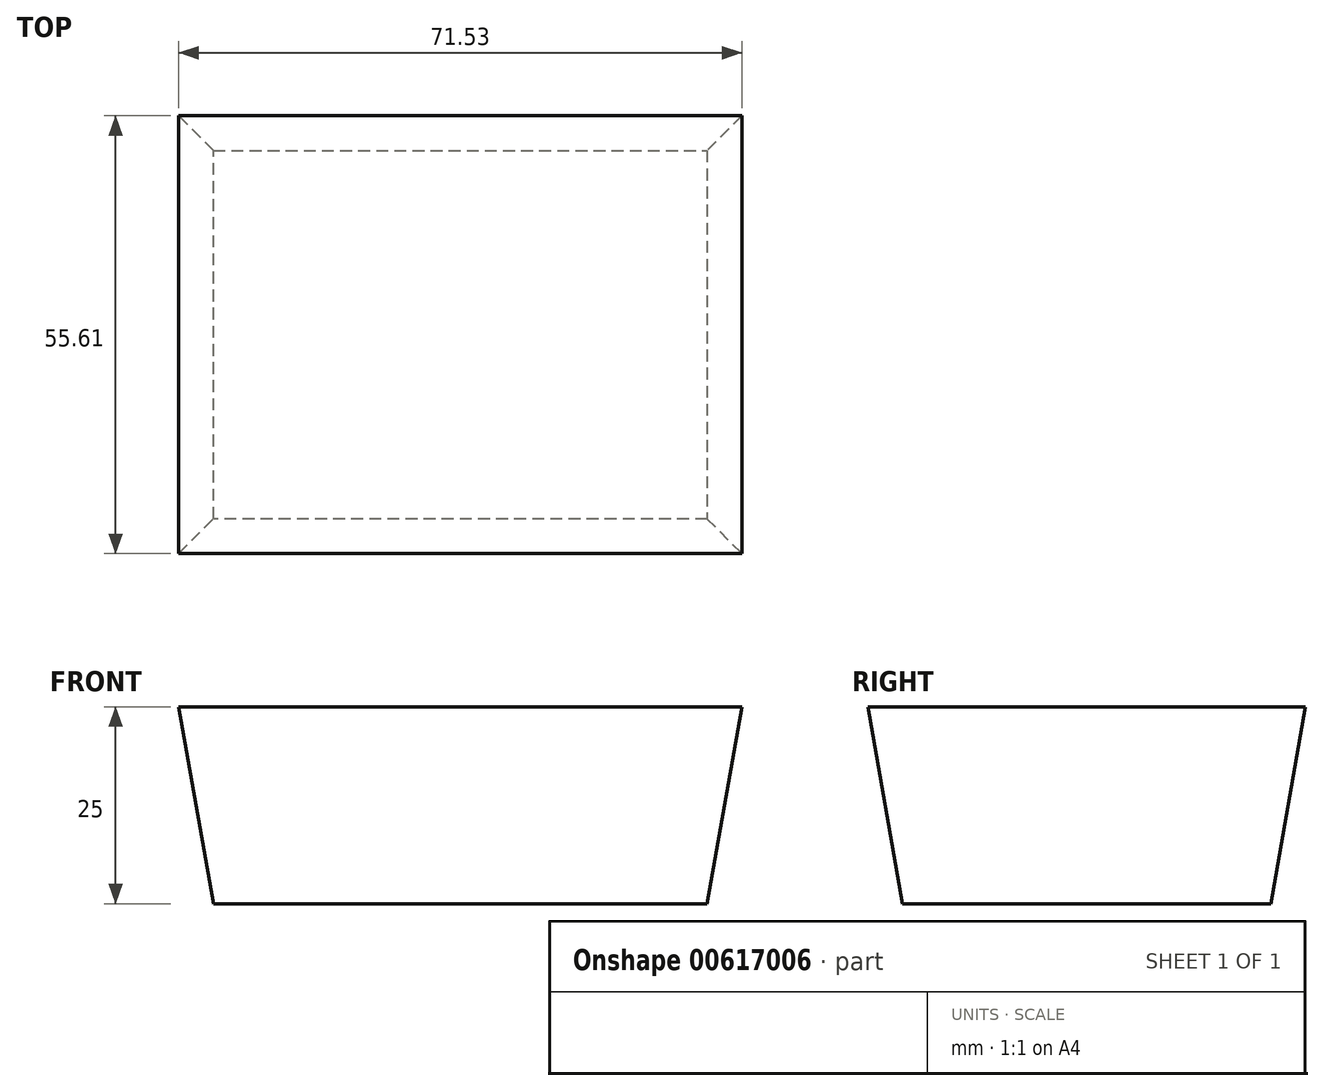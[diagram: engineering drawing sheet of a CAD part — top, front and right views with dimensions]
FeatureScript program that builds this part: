
annotation { "Feature Type Name" : "Feature", "Feature Type Description" : "" }
export const myFeature = defineFeature(function(context is Context, id is Id, definition is map)
    precondition{}
    {
        {
            var Q0;
            Q0=qCreatedBy(makeId("Top.planeOp"),FACE);
            var sketch = newSketch(context, id + "F0", { "sketchPlane" : qUnion([Q0])});
            skLineSegment(sketch, "E0.bottom", {"start": v(-32.52, 24.59) * mm, "end": v(30.2, 24.59) * mm});
            skLineSegment(sketch, "E0.top", {"start": v(-32.52, -22.2) * mm, "end": v(30.2, -22.2) * mm});
            skLineSegment(sketch, "E0.left", {"start": v(-32.52, 24.59) * mm, "end": v(-32.52, -22.2) * mm});
            skLineSegment(sketch, "E0.right", {"start": v(30.2, 24.59) * mm, "end": v(30.2, -22.2) * mm});
            skSolve(sketch);
        }
        {
            var Q0;
            Q0 = qSketchRegion(id + "F0", true);
            extrude(context, id + "F1", {"entities" : qUnion([Q0]), "depth" : 25 * mm, "offsetDistance" : 25 * mm, "hasDraft" : true, "draftAngle" : 10 * degree});
        }
    });
